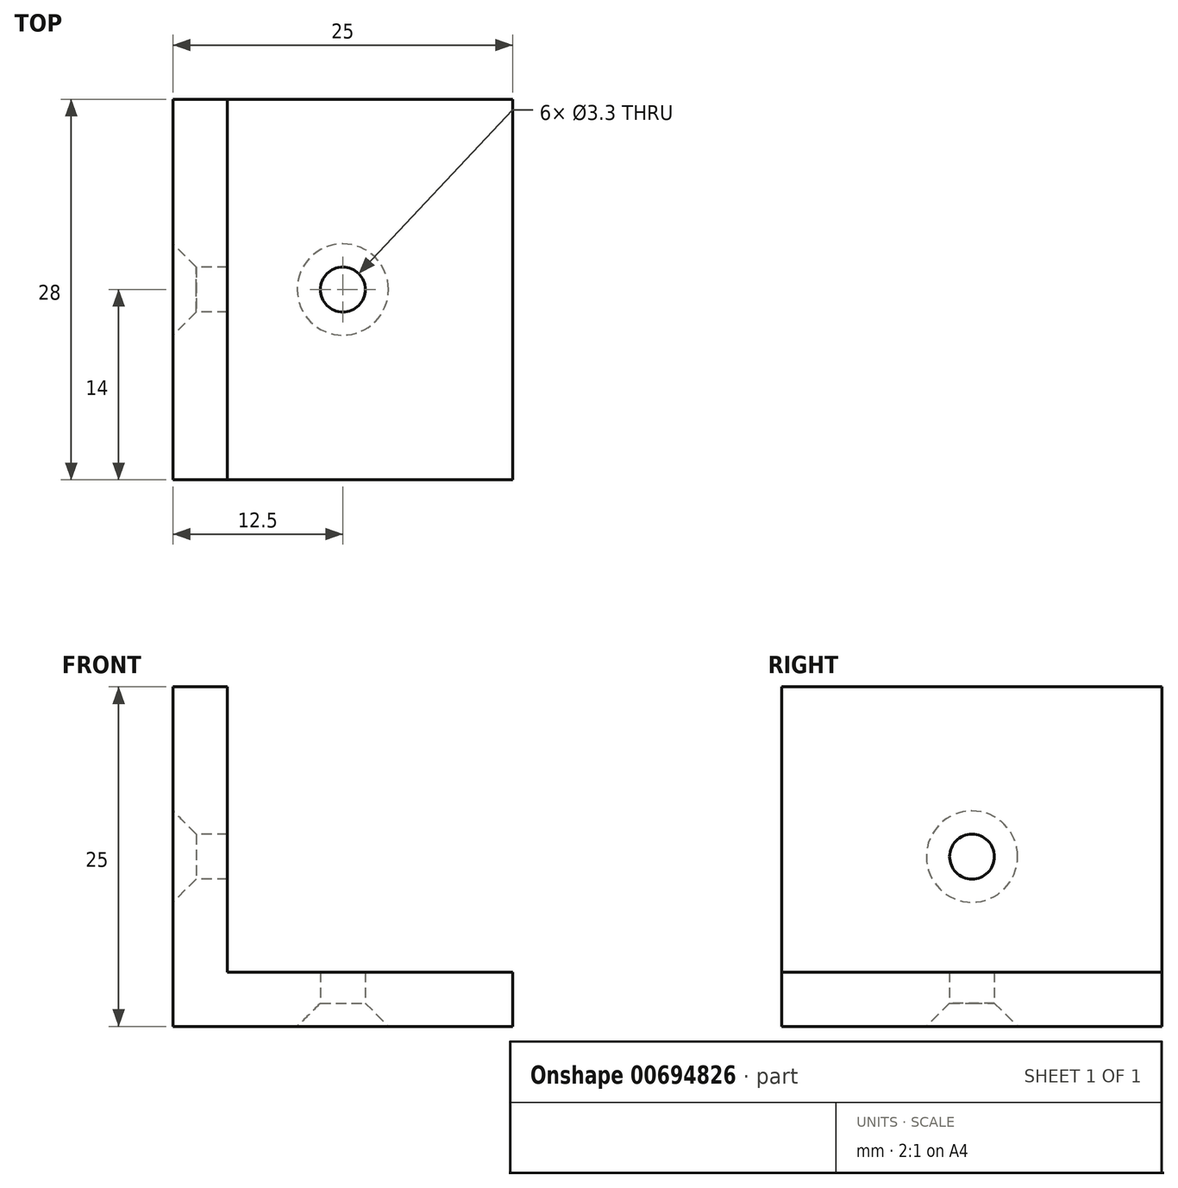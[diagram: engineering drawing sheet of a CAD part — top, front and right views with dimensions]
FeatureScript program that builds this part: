
annotation { "Feature Type Name" : "Feature", "Feature Type Description" : "" }
export const myFeature = defineFeature(function(context is Context, id is Id, definition is map)
    precondition{}
    {
        {
            var Q0;
            Q0=qCreatedBy(makeId("Front.planeOp"),FACE);
            var sketch = newSketch(context, id + "F0", { "sketchPlane" : qUnion([Q0])});
            skLineSegment(sketch, "E0.bottom", {"start": v(0, 0) * mm, "end": v(4, 0) * mm});
            skLineSegment(sketch, "E0.top", {"start": v(0, 25) * mm, "end": v(4, 25) * mm});
            skLineSegment(sketch, "E0.left", {"start": v(0, 0) * mm, "end": v(0, 25) * mm});
            skLineSegment(sketch, "E0.right", {"start": v(4, 4) * mm, "end": v(4, 25) * mm});
            skLineSegment(sketch, "E1.bottom", {"start": v(0, 0) * mm, "end": v(25, 0) * mm});
            skLineSegment(sketch, "E1.top", {"start": v(4, 4) * mm, "end": v(25, 4) * mm});
            skLineSegment(sketch, "E1.left", {"start": v(0, 0) * mm, "end": v(0, 4) * mm});
            skLineSegment(sketch, "E1.right", {"start": v(25, 0) * mm, "end": v(25, 4) * mm});
            skSolve(sketch);
        }
        {
            var Q0;
            Q0=qSketchRegion(id+"F0",true);
            extrude(context, id + "F1", {"entities" : qUnion([Q0]), "depth" : 28 * mm, "offsetDistance" : 25 * mm});
        }
        {
            var Q0;
            Q0=makeQuery(id+"F1.opExtrude","SWEPT_FACE",FACE,{"disambiguationData":[OSD([sQuery(id+"F0.wireOp",EDGE,"E0.left"),sQuery(id+"F0.wireOp",EDGE,"E1.left")])]});
            var sketch = newSketch(context, id + "F2", { "sketchPlane" : qUnion([Q0])});
            skLineSegment(sketch, "E2", {"start": v(0, 0) * mm, "end": v(28, 25) * mm});
            skPoint(sketch, "E3", {"position": v(14, 12.5) * mm});
            skSolve(sketch);
        }
        {
            var Q0;
            Q0=sQuery(id+"F2.wireOp",VERTEX,"E3");
            var Q1;
            Q1=makeQuery(id+"F1.opExtrude","SWEPT_BODY",BODY,{"disambiguationData":[OSD([sQuery(id+"F0.wireOp",EDGE,"E0.top"),sQuery(id+"F0.wireOp",EDGE,"E0.left"),sQuery(id+"F0.wireOp",EDGE,"E0.right"),sQuery(id+"F0.wireOp",EDGE,"E1.bottom"),sQuery(id+"F0.wireOp",EDGE,"E1.top"),sQuery(id+"F0.wireOp",EDGE,"E1.left"),sQuery(id+"F0.wireOp",EDGE,"E1.right")])]});
            hole(context, id + "F3", {"style" : HoleStyle.C_SINK, "endStyle" : HoleEndStyle.BLIND, "standardTappedOrClearance" : lookupTablePath({ "standard" : "ISO", "fit" : "Normal", "size" : "M3", "type" : "Clearance" }), "standardBlindInLast" : lookupTablePath({ "fit" : "Standard", "standard" : "ISO", "size" : "M3", "type" : "Clearance" }), "holeDiameter" : 3.3 * mm, "cSinkDiameter" : 6.72 * mm, "cSinkAngle" : 90 * degree, "majorDiameter" : 5 * mm, "holeDepth" : 40 * mm, "isTappedThrough" : true, "tappedDepth" : 12 * mm, "tapClearance" : 3, "locations" : qUnion([Q0]), "scope" : qUnion([Q1])});
        }
        {
            var Q0;
            Q0=makeQuery(id+"F1.opExtrude","SWEPT_FACE",FACE,{"disambiguationData":[OSD([sQuery(id+"F0.wireOp",EDGE,"E1.bottom")])]});
            var sketch = newSketch(context, id + "F4", { "sketchPlane" : qUnion([Q0])});
            skLineSegment(sketch, "E4", {"start": v(25, 0) * mm, "end": v(0, 28) * mm});
            skPoint(sketch, "E5", {"position": v(12.5, 14) * mm});
            skSolve(sketch);
        }
        {
            var Q0;
            Q0=sQuery(id+"F4.wireOp",VERTEX,"E5");
            var Q1;
            Q1=makeQuery(id+"F1.opExtrude","SWEPT_BODY",BODY,{"disambiguationData":[OSD([sQuery(id+"F0.wireOp",EDGE,"E0.top"),sQuery(id+"F0.wireOp",EDGE,"E0.left"),sQuery(id+"F0.wireOp",EDGE,"E0.right"),sQuery(id+"F0.wireOp",EDGE,"E1.bottom"),sQuery(id+"F0.wireOp",EDGE,"E1.top"),sQuery(id+"F0.wireOp",EDGE,"E1.left"),sQuery(id+"F0.wireOp",EDGE,"E1.right")])]});
            hole(context, id + "F5", {"style" : HoleStyle.C_SINK, "endStyle" : HoleEndStyle.BLIND, "standardTappedOrClearance" : lookupTablePath({ "standard" : "ISO", "fit" : "Normal", "size" : "M3", "type" : "Clearance" }), "standardBlindInLast" : lookupTablePath({ "fit" : "Standard", "standard" : "ISO", "size" : "M3", "type" : "Clearance" }), "holeDiameter" : 3.3 * mm, "cSinkDiameter" : 6.72 * mm, "cSinkAngle" : 90 * degree, "majorDiameter" : 5 * mm, "holeDepth" : 40 * mm, "isTappedThrough" : true, "tappedDepth" : 12 * mm, "tapClearance" : 3, "locations" : qUnion([Q0]), "scope" : qUnion([Q1])});
        }
    });
